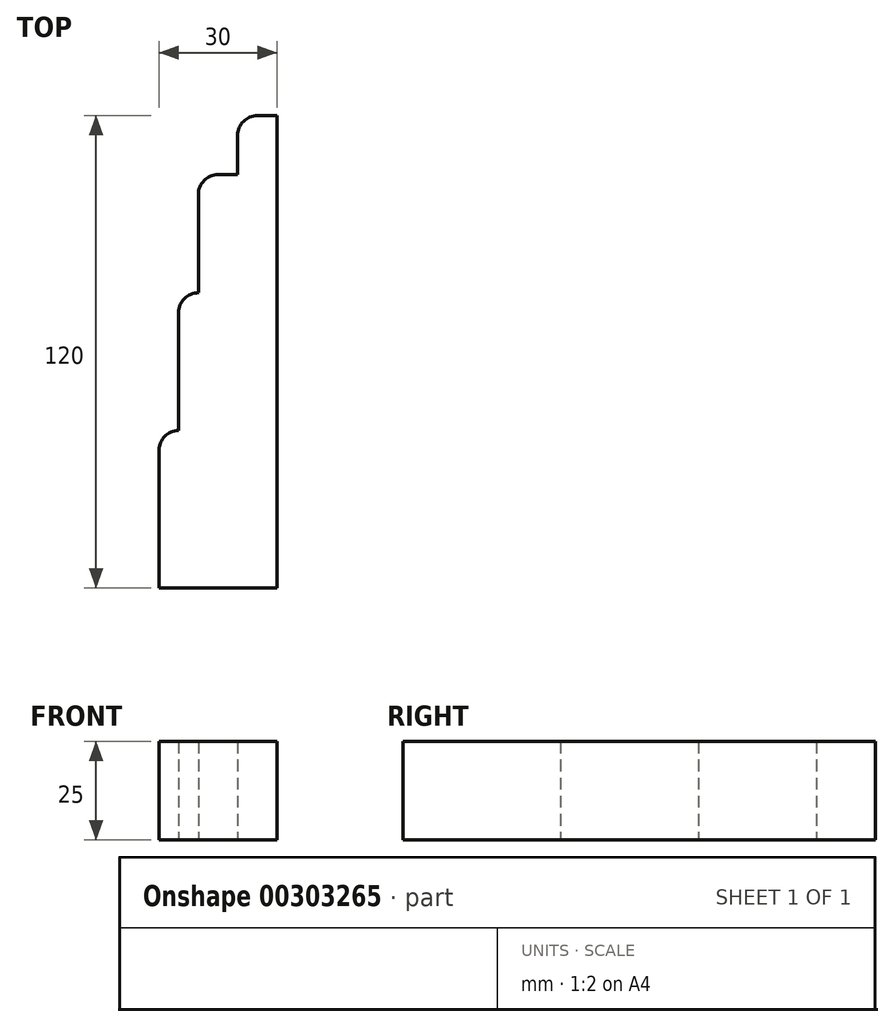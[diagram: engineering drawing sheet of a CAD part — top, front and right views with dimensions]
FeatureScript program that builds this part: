
annotation { "Feature Type Name" : "Feature", "Feature Type Description" : "" }
export const myFeature = defineFeature(function(context is Context, id is Id, definition is map)
    precondition{}
    {
        {
            var Q0;
            Q0=qCreatedBy(makeId("Top.planeOp"),FACE);
            var sketch = newSketch(context, id + "F0", { "sketchPlane" : qUnion([Q0])});
            skLineSegment(sketch, "E0", {"start": v(-20.37, 56.99) * mm, "end": v(-20.37, -63.01) * mm});
            skLineSegment(sketch, "E1", {"start": v(-50.37, -63.01) * mm, "end": v(-20.37, -63.01) * mm});
            skLineSegment(sketch, "E2", {"start": v(-50.37, -63.01) * mm, "end": v(-50.37, -28.01) * mm});
            skLineSegment(sketch, "E3", {"start": v(-45.37, -23.01) * mm, "end": v(-45.37, -23.01) * mm});
            skLineSegment(sketch, "E4", {"start": v(-45.37, -23.01) * mm, "end": v(-45.37, 6.99) * mm});
            skLineSegment(sketch, "E5", {"start": v(-40.37, 11.99) * mm, "end": v(-40.37, 11.99) * mm});
            skLineSegment(sketch, "E6", {"start": v(-40.37, 11.99) * mm, "end": v(-40.37, 36.99) * mm});
            skLineSegment(sketch, "E7", {"start": v(-35.37, 41.99) * mm, "end": v(-30.37, 41.99) * mm});
            skLineSegment(sketch, "E8", {"start": v(-20.37, 56.99) * mm, "end": v(-25.37, 56.99) * mm});
            skLineSegment(sketch, "E9", {"start": v(-30.37, 51.99) * mm, "end": v(-30.37, 41.99) * mm});
            skPoint(sketch, "E10.visualSharp", {"position": v(-30.37, 56.99) * mm});
            skArc(sketch, "E10.filletArc", {"start": v(-25.37, 56.99) * mm, "mid": v(-28.9, 55.52) * mm, "end": v(-30.37, 51.99) * mm});
            skPoint(sketch, "E11.visualSharp", {"position": v(-40.37, 41.99) * mm});
            skArc(sketch, "E11.filletArc", {"start": v(-35.37, 41.99) * mm, "mid": v(-38.9, 40.52) * mm, "end": v(-40.37, 36.99) * mm});
            skPoint(sketch, "E12.visualSharp", {"position": v(-45.37, 11.99) * mm});
            skArc(sketch, "E12.filletArc", {"start": v(-40.37, 11.99) * mm, "mid": v(-43.9, 10.52) * mm, "end": v(-45.37, 6.99) * mm});
            skPoint(sketch, "E13.visualSharp", {"position": v(-50.37, -23.01) * mm});
            skArc(sketch, "E13.filletArc", {"start": v(-45.37, -23.01) * mm, "mid": v(-48.9, -24.48) * mm, "end": v(-50.37, -28.01) * mm});
            skSolve(sketch);
        }
        {
            var Q0;
            Q0 = qSketchRegion(id + "F0", true);
            extrude(context, id + "F1", {"entities" : qUnion([Q0]), "depth" : 25 * mm});
        }
    });
